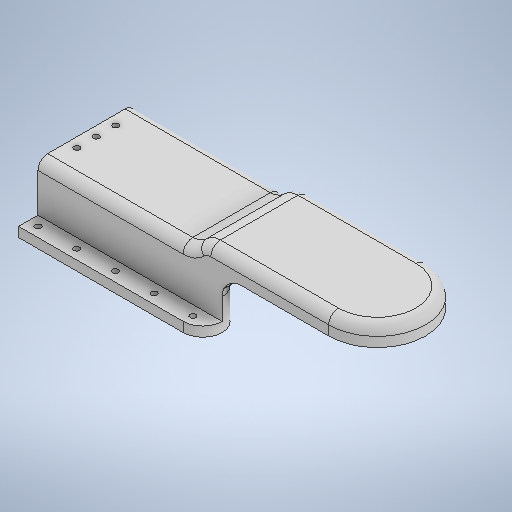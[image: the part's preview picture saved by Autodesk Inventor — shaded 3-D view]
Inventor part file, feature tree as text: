
AUTODESK INVENTOR PART (.ipt)
format: ipt  version: 2025 (Build 290162000, 162)  size: 375,296 bytes
history: native  units: mm
features: sketch x8, extrude x6, fillet x5
ambient origin geometry x8: Origin, YZ Plane, XZ Plane, XY Plane, X Axis, Y Axis, Z Axis, Center Point
bodies: Solid1 (feature_tree)
feature tree (19):
  extrude  "Extrusion1"  Depth=80.0mm
  fillet  "Fillet1"  Radius=26.0mm
  extrude  "Extrusion2"  Depth=10.0mm
  extrude  "Extrusion3"  Depth=10.0mm
  extrude  "Extrusion4"  TaperAngle=0.0deg  [1 undecoded]
  extrude  "Extrusion7"  Depth=30.0mm
  sketch  "Sketch11"  dims[d45=5.1mm d46=5.1mm d47=10.0mm d48=0.0mm d50=3.1mm d51=10.0mm d52=30.0mm d54=10.0mm d55=10.0mm d57=10.0mm d59=25.0mm d60=10.0mm d61=0.0mm d62=15.0mm d63=160.0mm d64=10.0mm d65=5.0mm d67=10.0mm d68=10.0mm d69=30.0mm d66=0.5mm]
  fillet  "Fillet2"  Radius=6.0mm
  extrude  "Extrusion8"  Depth=5.0mm
  fillet  "Fillet3"  Radius=5.0mm
  fillet  "Fillet4"  Radius=5.0mm
  fillet  "Fillet6"  Radius=5.1mm
  sketch  "Sketch1"  dims[d2=80.0mm d4=80.0mm d5=26.0mm]
  sketch  "Sketch2"  dims[d9=10.0mm d10=10.0mm]
  sketch  "Sketch3"  dims[d11=10.0mm d12=0.0mm d13=0.0mm]
  sketch  "Sketch4"  dims[d18=10.0mm d19=3.1mm d20=5.0mm]
  sketch  "Sketch Rectangular Pattern1"  dims[d6=50.0mm d7=0.0mm d8=10.0mm]
  sketch  "Sketch9"  dims[d21=50.0mm d23=20.0mm d24=10.0mm d26=10.0mm d28=5.0mm d29=0.0mm d44=5.1mm]
  sketch  "Sketch Rectangular Pattern3"  dims[d14=20.2mm d15=30.0mm d16=6.0mm d17=0.0mm]
note: 1 required parameter value undecoded (feature->parameter linkage not recoverable at this tier; creation-order binding heuristic only, values carry confidence <= 0.55)
